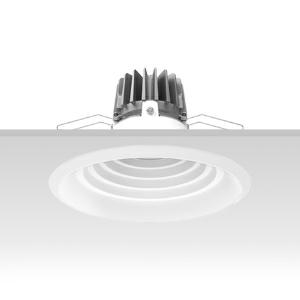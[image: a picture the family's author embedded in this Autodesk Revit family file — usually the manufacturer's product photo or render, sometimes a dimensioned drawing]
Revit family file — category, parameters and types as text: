
# Revit family: 3f_filippi_-_3f_reno_bianco_ampio_3f_filippi_-_30675_-_3f_reno_200_wh_2000-930_dali_wide
name_source: partatom
category: Lighting Fixtures
units: mm (PartAtom-declared; Revit-internal decimal feet)

## family parameters
Cut with Voids When Loaded = No
Host = Face
Light Source = No
Part Type = Normal
Room Calculation Point = No
Round Connector Dimension = Use Diameter
Shared = No

## types (1)
- 3F Filippi - 3F Reno Bianco Ampio (1 x LED, 1880 lm, 24 W, 3000 K)
    Apparent Load = 24 VA
    Approval mark = CE
    CIE Flux Codes = 80 97 100 100 100
    Color Rendering = 90
    Color Temperature = 3000 K
    Control Gear = Electronic transformer
    Default Elevation = 1800 mm
    Description = ILLUMINOTECHNICAL
Luminous efficiency 100% (DLOR 100%, ULOR 0%).
Initial luminous flux of the luminaire 1880 lm.
Direct symmetric wide distribution.
Installation Interdistance Transv.D = 1.56 x hu - Long.D = 1.56 x hu.
Average luminance <3000 cd/m² for radial angles >65°.
Tabular UGR (CIE 117 - 4H-8H; S=0.25H; 70/50/20): RUG 19.2 - 19.2.
Beam angle: 85° - 84°.
Luminous efficacy 78 lm/W.
Lifetime (L90/B10): 30000 h. (tq+25°C)
Lifetime (L85/B10): 50000 h. (tq+25°C)
Lifetime (L70/B10): 80000 h. (tq+25°C)
Sudden decreased luminous flux after 50000 hours: 0% (C0).
Photobiological safety in compliance with IEC/TR 62778: RG0 risk exempt, (IEC 62471).
In compliance with IEC/EN 62722-2-1 - IEC/EN 62717 standards.

SOURCE
Compact LED module 2000/930.
Energy efficiency class (UE 2019/2020 - UE 2019/2015): E.
CIE 13.3 Colour rendering index: CRI >90 (R9 >50%).
IES TM-30 Fidelity Index: Rf = 92 Rg = 101.
CCT nominal colour temperature 3000 K.
Colour initial tolerance (MacAdam): SDCM 3.
Zhaga Book 3 compliant.

MECHANICAL
Passive heat dissipator in die-casting aluminium, oversized, for optimum thermal management of the LED module.
Parabolic element with graduated/concentric rings in white polycarbonate.
Transparent external lens with glossy and satin differentiated surfaces, with a cooling and anti-insect system in methacrylate (PMMA).
Fastening spring clips in stainless steel.
Dimensions: diameter 216 mm, height 142 mm. Weight 0.84 kg.
IP44 protection degree for exposed part, IP20 for recessed part.
Mechanical strength to impacts IK04 (0.5 joule).
Glow-wire test resistance 650°C.

ELECTRICAL
Wiring on a separate unit.
Halogen Free DALI-2 DATI (Parts 251, 252, 253), PUSH-DIM, electronic wiring 230V-50/60Hz, power factor 0.95 at full load, THD <25%, constant output current, SELV, class II, 1 driver, 1 DALI addresse.
Power of the luminaire 24 W.
ENEC - CE.
SAFE FLICKER: PstLM=<1 and SVM=<0.4 (IEC TR 61547-1 and IEC TR 63158), to ensure a more comfortable and safe light.
Luminaire compliant with EN 60598-2-22 for power supply from a centralised emergency system CPSS (Central Power Supply System), not incorporated in the luminaire - high risk areas excluded. The default power and flux are 100% in AC and 100% in DC.
Ambient temperature from 0°C to +25°C.
Temperature class T6 max 85°C.
Relative humidity UR: <85%.

INSTALLATION
Pull-up recessed fitting.
False ceiling carving: 200 mm.
All accessories dedicated to this product are available on the Catalog and on our website www.3F-Filippi.com.

APPLICATIONS
Environments: architectural, commercial, exhibition areas, transit areas, corridors, shops, display windows, service areas.
In false ceilings with narrow voids.

LIGHT MANAGEMENT
Recommended minimum setting: 10%.
The luminaire, equipped with (DALI-2 DATI) driver, can be controlled manually with 3F Easy Dim technology or automatically/manually with wired or wireless DALI/D2D control systems.
The D2D driver guarantees interoperability with other devices with the same certification by making the following information available:
Device Data (Part 251), Energy Report (Part 252), Diagnosis & Maintenance (Part 253).
In electrical systems without a regulation system (manual or automatic) and DALI bus, a suitable jumper must be made on the DA-DA terminals of the appliance.

WARNING
Luminaire designed for disposal/recycling at end-of-life.
Replaceable (LED only) light source by a professional. Replaceable control gear by a professional.
    Height = 0 mm  [stored 0 ft]
    Lamp = 1 x LED
    Lamp Light Flux = 1880 lm
    Lamp Power = 24 W
    Lamp count = 1
    Length = 216 mm
    Lifetime = 50000 h
    Luminous efficacy = 78 lm/W
    Manufacturer = 3F Filippi
    ModVariant = No
    Model = 3F Filippi - 30675 - 3F Reno 200 WH 2000-930 DALI WIDE
    Mounting Place = Ceiling
    Mounting Type = Recessed
    Number of Poles = 1
    OnlyDefault = Yes
    Power Factor = 1
    Product Name = 3F Filippi - 3F Reno Bianco Ampio
    Product group = recessed luminaire
    ProductGroupID = 4
    Protection Class = Protection class II
    Protection Degree = IP 20
    RLX_Detail_Level = 1
    RLX_Emergency_Light_Flux = 0 lm
    RLX_Emergency_Type = 0
    RLX_Emergency_Type_DB = No
    RlxData = <blob elided: 91541 chars, md5=28521723>
    Socket = socket
    Standby Power = 0 W
    System Light Flux = 1880 lm
    System Power = 24 W
    Type Comments = Product without accessories
    Type Image = 3ffilippi_3f_reno_200_wh_2000.jpg
    URL = http://relux.com
    VarID = ---
    Voltage = 0 V
    Weight = 0.00 kg
    Width = 0 mm  [stored 0 ft]

note: [stored X ft] marks values corroborated as IEEE doubles in the binary element streams (Revit-internal decimal feet)

## geometry (parser evidence)
native form markers: Blend x4, Sweep x10
no freeform markers — native parametric forms only
